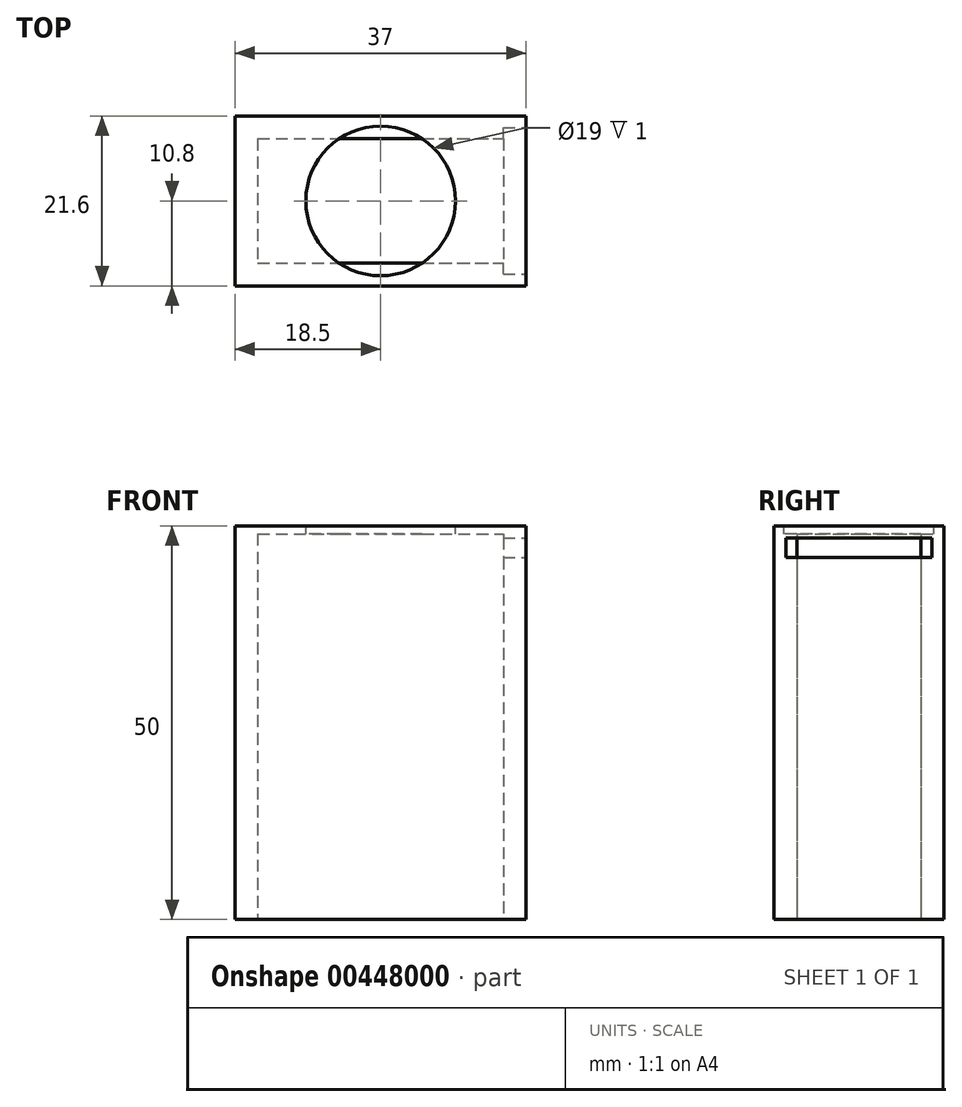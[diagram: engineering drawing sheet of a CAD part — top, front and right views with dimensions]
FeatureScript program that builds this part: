
annotation { "Feature Type Name" : "Feature", "Feature Type Description" : "" }
export const myFeature = defineFeature(function(context is Context, id is Id, definition is map)
    precondition{}
    {
        {
            var Q0;
            Q0=qCreatedBy(makeId("Top.planeOp"),FACE);
            var sketch = newSketch(context, id + "F0", { "sketchPlane" : qUnion([Q0])});
            skLineSegment(sketch, "E0.bottom", {"start": v(-18.5, 10.8) * mm, "end": v(18.5, 10.8) * mm});
            skLineSegment(sketch, "E0.top", {"start": v(-18.5, -10.8) * mm, "end": v(18.5, -10.8) * mm});
            skLineSegment(sketch, "E0.left", {"start": v(-18.5, 10.8) * mm, "end": v(-18.5, -10.8) * mm});
            skLineSegment(sketch, "E0.right", {"start": v(18.5, 10.8) * mm, "end": v(18.5, -10.8) * mm});
            skPoint(sketch, "E0.middle", {"position": v(0, 0) * mm});
            skSolve(sketch);
        }
        {
            var Q0;
            Q0=qCreatedBy(makeId("Top.planeOp"),FACE);
            cPlane(context, id + "F1", {"entities" : qUnion([Q0]), "cplaneType" : CPlaneType.OFFSET, "offset" : 50 * mm, "width" : 150 * mm, "height" : 150 * mm});
        }
        {
            var Q0;
            Q0=qCreatedBy(id+"F1.planeOp",FACE);
            var sketch = newSketch(context, id + "F2", { "sketchPlane" : qUnion([Q0])});
            skLineSegment(sketch, "E1.bottom", {"start": v(18.5, -10.8) * mm, "end": v(-18.5, -10.8) * mm});
            skLineSegment(sketch, "E1.top", {"start": v(18.5, 10.8) * mm, "end": v(-18.5, 10.8) * mm});
            skLineSegment(sketch, "E1.left", {"start": v(18.5, -10.8) * mm, "end": v(18.5, 10.8) * mm});
            skLineSegment(sketch, "E1.right", {"start": v(-18.5, -10.8) * mm, "end": v(-18.5, 10.8) * mm});
            skPoint(sketch, "E1.middle", {"position": v(0, 0) * mm});
            skSolve(sketch);
        }
        {
            var Q0;
            Q0=qCreatedBy(makeId("Front.planeOp"),FACE);
            cPlane(context, id + "F3", {"entities" : qUnion([Q0]), "cplaneType" : CPlaneType.OFFSET, "offset" : 10.8 * mm, "width" : 150 * mm, "height" : 150 * mm});
        }
        {
            var Q0;
            Q0=makeQuery(id+"F0.imprint","IMPRINT",FACE,{"disambiguationData":[TD([[makeQuery(id+"F0.imprint","IMPRINT",EDGE,{"derivedFrom":sQuery(id+"F0.wireOp",EDGE,"E0.bottom")}),-1.0]])]});
            extrude(context, id + "F4", {"entities" : qUnion([Q0]), "depth" : 50 * mm});
        }
        {
            var Q0;
            Q0=makeQuery(id+"F4.opExtrude","CAP_FACE",FACE,{"disambiguationData":[OSD([sQuery(id+"F0.wireOp",EDGE,"E0.bottom"),sQuery(id+"F0.wireOp",EDGE,"E0.top"),sQuery(id+"F0.wireOp",EDGE,"E0.left"),sQuery(id+"F0.wireOp",EDGE,"E0.right")])],"isStart":false});
            var Q1;
            Q1=makeQuery(id+"F4.opExtrude","CAP_FACE",FACE,{"disambiguationData":[OSD([sQuery(id+"F0.wireOp",EDGE,"E0.bottom"),sQuery(id+"F0.wireOp",EDGE,"E0.top"),sQuery(id+"F0.wireOp",EDGE,"E0.left"),sQuery(id+"F0.wireOp",EDGE,"E0.right")])],"isStart":true});
            shell(context, id + "F5", {"entities" : qUnion([Q0, Q1]), "thickness" : 2.9 * mm});
        }
        {
            var Q0;
            Q0=makeQuery(id+"F4.opExtrude","SWEPT_FACE",FACE,{"disambiguationData":[OSD([sQuery(id+"F0.wireOp",EDGE,"E0.right")])]});
            var sketch = newSketch(context, id + "F6", { "sketchPlane" : qUnion([Q0])});
            skLineSegment(sketch, "E2.bottom", {"start": v(-10.8, 50) * mm, "end": v(10.8, 50) * mm});
            skLineSegment(sketch, "E2.top", {"start": v(-10.8, 44.5) * mm, "end": v(10.8, 44.5) * mm});
            skLineSegment(sketch, "E2.left", {"start": v(-10.8, 50) * mm, "end": v(-10.8, 44.5) * mm});
            skLineSegment(sketch, "E2.right", {"start": v(10.8, 50) * mm, "end": v(10.8, 44.5) * mm});
            skLineSegment(sketch, "E3.0", {"start": v(-9.3, 46) * mm, "end": v(9.3, 46) * mm});
            skLineSegment(sketch, "E3.1", {"start": v(-9.3, 48.5) * mm, "end": v(-9.3, 46) * mm});
            skLineSegment(sketch, "E3.2", {"start": v(-9.3, 48.5) * mm, "end": v(9.3, 48.5) * mm});
            skLineSegment(sketch, "E3.3", {"start": v(9.3, 48.5) * mm, "end": v(9.3, 46) * mm});
            skSolve(sketch);
        }
        {
            var Q0;
            Q0=makeQuery(id+"F6.imprint","IMPRINT",FACE,{"disambiguationData":[TD([[makeQuery(id+"F6.imprint","IMPRINT",EDGE,{"derivedFrom":sQuery(id+"F6.wireOp",EDGE,"E3.0")}),1.0]])]});
            extrude(context, id + "F7", {"entities" : qUnion([Q0]), "operationType" : NewBodyOperationType.REMOVE, "oppositeDirection" : true, "depth" : 2.9 * mm});
        }
        {
            var Q0;
            Q0=qCreatedBy(id+"F1.planeOp",FACE);
            var sketch = newSketch(context, id + "F8", { "sketchPlane" : qUnion([Q0])});
            skLineSegment(sketch, "E4.bottom", {"start": v(-18.5, 10.8) * mm, "end": v(18.5, 10.8) * mm});
            skLineSegment(sketch, "E4.top", {"start": v(-18.5, -10.8) * mm, "end": v(18.5, -10.8) * mm});
            skLineSegment(sketch, "E4.left", {"start": v(-18.5, 10.8) * mm, "end": v(-18.5, -10.8) * mm});
            skLineSegment(sketch, "E4.right", {"start": v(18.5, 10.8) * mm, "end": v(18.5, -10.8) * mm});
            skSolve(sketch);
        }
        {
            var Q0;
            Q0 = qSketchRegion(id + "F8", true);
            extrude(context, id + "F9", {"entities" : qUnion([Q0]), "operationType" : NewBodyOperationType.ADD, "oppositeDirection" : true, "depth" : 1 * mm});
        }
        {
            var Q0;
            Q0=sQuery(id+"F2.wireOp",VERTEX,"E1.middle");
            var Q1;
            Q1=makeQuery(id+"F4.opExtrude","SWEPT_BODY",BODY,{"disambiguationData":[OSD([sQuery(id+"F0.wireOp",EDGE,"E0.bottom"),sQuery(id+"F0.wireOp",EDGE,"E0.top"),sQuery(id+"F0.wireOp",EDGE,"E0.left"),sQuery(id+"F0.wireOp",EDGE,"E0.right")])]});
            hole(context, id + "F10", {"style" : HoleStyle.C_BORE, "endStyle" : HoleEndStyle.THROUGH, "holeDiameter" : 15.5 * mm, "cBoreDiameter" : 19 * mm, "cBoreDepth" : 1 * mm, "isTappedThrough" : true, "tappedDepth" : 12 * mm, "tapClearance" : 3, "startFromSketch" : true, "locations" : qUnion([Q0]), "scope" : qUnion([Q1])});
        }
    });
